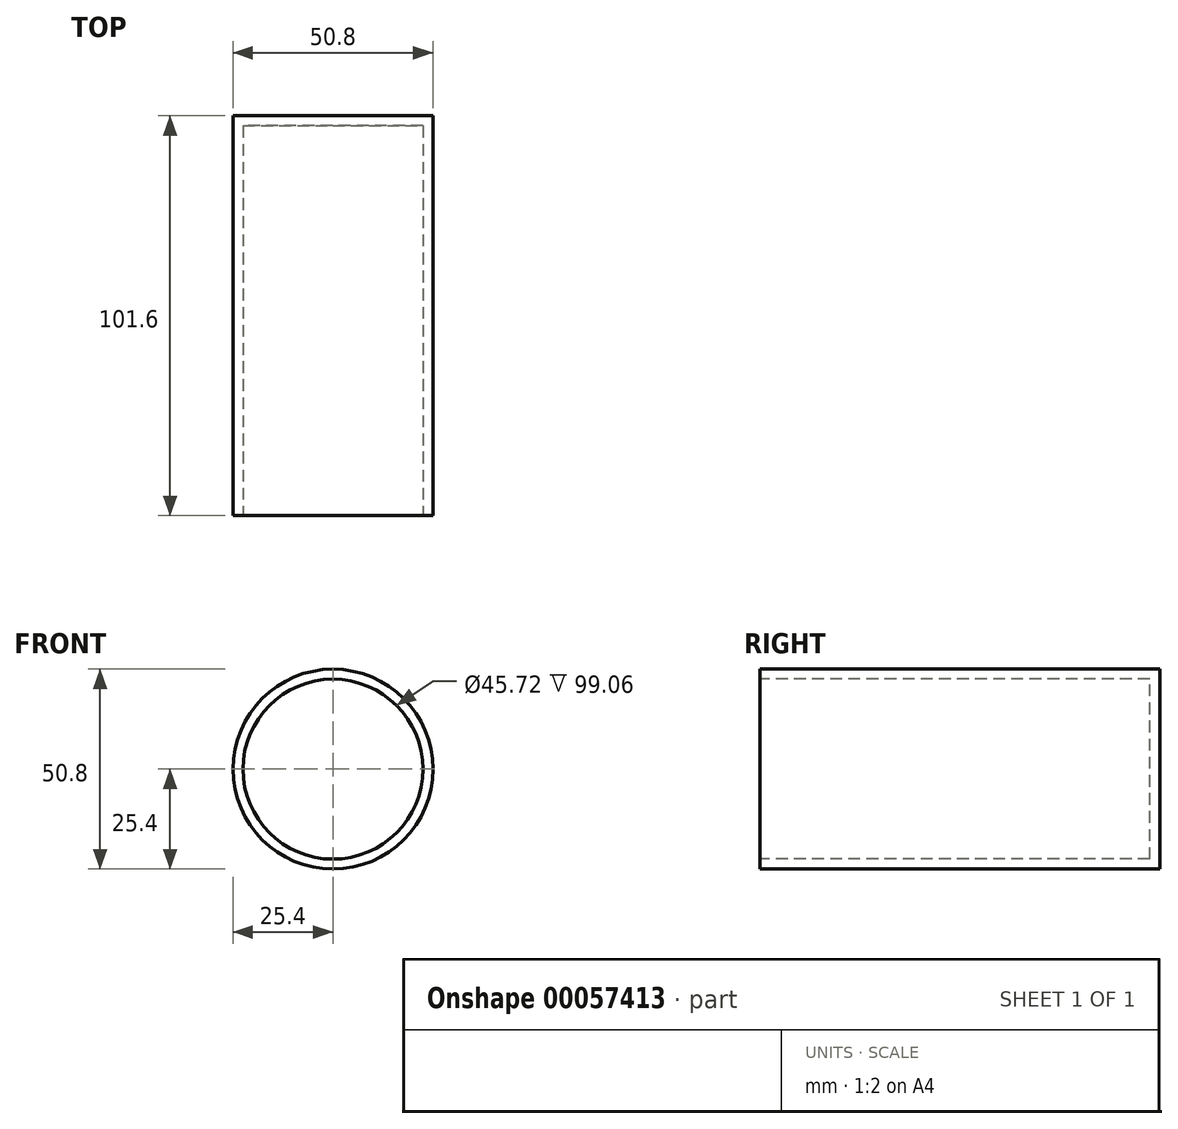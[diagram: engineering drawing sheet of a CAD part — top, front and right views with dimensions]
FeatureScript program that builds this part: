
annotation { "Feature Type Name" : "Feature", "Feature Type Description" : "" }
export const myFeature = defineFeature(function(context is Context, id is Id, definition is map)
    precondition{}
    {
        {
            var Q0;
            Q0=qCreatedBy(makeId("Front.planeOp"),FACE);
            var sketch = newSketch(context, id + "F0", { "sketchPlane" : qUnion([Q0])});
            skCircle(sketch, "E0", {"center": v(0, 0) * mm, "radius": 25.4 * mm});
            skSolve(sketch);
        }
        {
            var Q0;
            Q0 = qSketchRegion(id + "F0", true);
            var Q1;
            Q1=sQuery(id+"F0.wireOp",EDGE,"E0");
            extrude(context, id + "F1", {"entities" : qUnion([Q0]), "surfaceEntities" : qUnion([Q1]), "oppositeDirection" : true, "depth" : 101.6 * mm});
        }
        {
            var Q0;
            Q0=makeQuery(id+"F1.opExtrude","CAP_FACE",FACE,{"disambiguationData":[OSD([sQuery(id+"F0.wireOp",EDGE,"E0")])],"isStart":true});
            shell(context, id + "F2", {"entities" : qUnion([Q0]), "thickness" : 2.54 * mm});
        }
    });
